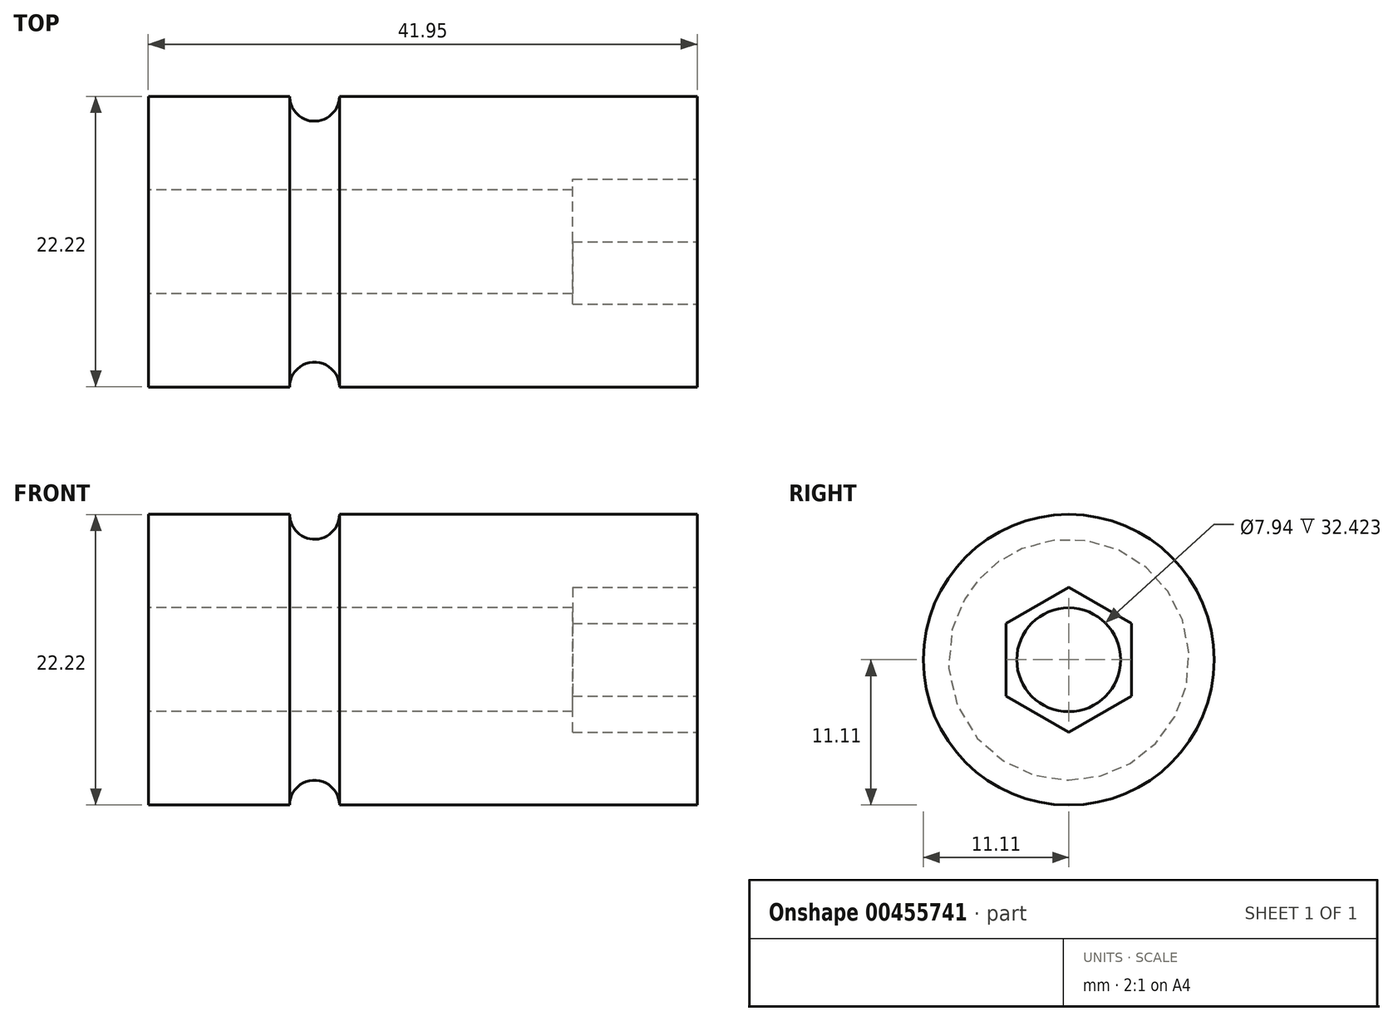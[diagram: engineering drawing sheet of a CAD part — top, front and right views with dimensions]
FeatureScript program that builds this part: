
annotation { "Feature Type Name" : "Feature", "Feature Type Description" : "" }
export const myFeature = defineFeature(function(context is Context, id is Id, definition is map)
    precondition{}
    {
        {
            var Q0;
            Q0=qCreatedBy(makeId("Right.planeOp"),FACE);
            var sketch = newSketch(context, id + "F0", { "sketchPlane" : qUnion([Q0])});
            skCircle(sketch, "E0", {"center": v(0, 0) * mm, "radius": 11.11 * mm});
            skPoint(sketch, "E1.0.midPoint", {"position": v(4.79, 0) * mm});
            skSolve(sketch);
        }
        {
            var Q0;
            Q0 = qSketchRegion(id + "F0", true);
            extrude(context, id + "F1", {"entities" : qUnion([Q0]), "oppositeDirection" : true, "depth" : 41.95 * mm});
        }
        {
            var Q0;
            Q0=qCreatedBy(makeId("Right.planeOp"),FACE);
            var sketch = newSketch(context, id + "F2", { "sketchPlane" : qUnion([Q0])});
            skCircle(sketch, "E2.cCircle", {"center": v(0, 0) * mm, "radius": 4.79 * mm, "construction": true});
            skLineSegment(sketch, "E2.0", {"start": v(4.79, 2.76) * mm, "end": v(4.79, -2.76) * mm});
            skLineSegment(sketch, "E2.1", {"start": v(4.79, -2.76) * mm, "end": v(0, -5.53) * mm});
            skLineSegment(sketch, "E2.2", {"start": v(0, -5.53) * mm, "end": v(-4.79, -2.76) * mm});
            skLineSegment(sketch, "E2.3", {"start": v(-4.79, -2.76) * mm, "end": v(-4.79, 2.76) * mm});
            skLineSegment(sketch, "E2.4", {"start": v(-4.79, 2.76) * mm, "end": v(0, 5.53) * mm});
            skLineSegment(sketch, "E2.5", {"start": v(0, 5.53) * mm, "end": v(4.79, 2.76) * mm});
            skPoint(sketch, "E2.0.midPoint", {"position": v(4.79, 0) * mm});
            skSolve(sketch);
        }
        {
            var Q0;
            Q0 = qSketchRegion(id + "F2", true);
            extrude(context, id + "F3", {"entities" : qUnion([Q0]), "operationType" : NewBodyOperationType.REMOVE, "oppositeDirection" : true, "depth" : 9.52 * mm});
        }
        {
            var Q0;
            Q0=makeQuery(id+"F1.opExtrude","CAP_FACE",FACE,{"disambiguationData":[OSD([sQuery(id+"F0.wireOp",EDGE,"E0")])],"isStart":false});
            var sketch = newSketch(context, id + "F4", { "sketchPlane" : qUnion([Q0])});
            skPoint(sketch, "E3", {"position": v(0, 0) * mm});
            skSolve(sketch);
        }
        {
            var Q0;
            Q0=sQuery(id+"F4.wireOp",VERTEX,"E3");
            var Q1;
            Q1=makeQuery(id+"F1.opExtrude","SWEPT_BODY",BODY,{"disambiguationData":[OSD([sQuery(id+"F0.wireOp",EDGE,"E0")])]});
            hole(context, id + "F5", {"style" : HoleStyle.SIMPLE, "endStyle" : HoleEndStyle.BLIND, "standardTappedOrClearance" : lookupTablePath({ "standard" : "ANSI", "engagement" : "75%", "pitch" : "16 tpi", "size" : "3/8", "type" : "Tapped" }), "standardBlindInLast" : lookupTablePath({ "standard" : "ANSI", "engagement" : "75%", "pitch" : "16 tpi", "size" : "3/8", "type" : "Tapped" }), "holeDiameter" : 7.94 * mm, "showTappedDepth" : true, "holeDepth" : 34.75 * mm, "isTappedThrough" : true, "tappedDepth" : 29.98 * mm, "tapClearance" : 3, "locations" : qUnion([Q0]), "scope" : qUnion([Q1]), "majorDiameter" : 9.53 * mm});
        }
        {
            var Q0;
            Q0=qCreatedBy(makeId("Front.planeOp"),FACE);
            var sketch = newSketch(context, id + "F6", { "sketchPlane" : qUnion([Q0])});
            skCircle(sketch, "E4", {"center": v(-29.25, 11.11) * mm, "radius": 1.9 * mm});
            skLineSegment(sketch, "E5", {"start": v(0, 0) * mm, "end": v(-64.29, 0) * mm, "construction": true});
            skSolve(sketch);
        }
        {
            var Q0;
            Q0=makeQuery(id+"F6.imprint","IMPRINT",FACE,{"disambiguationData":[TD([[makeQuery(id+"F6.imprint","IMPRINT",EDGE,{"derivedFrom":sQuery(id+"F6.wireOp",EDGE,"E4")}),1.0]])]});
            var Q1;
            Q1=sQuery(id+"F6.wireOp",EDGE,"E5");
            var Q2;
            Q2=sQuery(id+"F6.wireOp",EDGE,"E5");
            revolve(context, id + "F7", {"operationType" : NewBodyOperationType.REMOVE, "entities" : qUnion([Q0]), "surfaceEntities" : qUnion([Q1]), "axis" : qUnion([Q2]), "revolveType" : RevolveType.FULL, "oppositeDirection" : true});
        }
    });
